FCSTD DOCUMENT  (FreeCAD 1.1R39747 (Git))
Label: Hackrf-side
License: All rights reserved
LicenseURL: https://en.wikipedia.org/wiki/All_rights_reserved
objects: Sketcher::SketchObject×3, PartDesign::Body×2, App::Point×2
note: 8 computed .brp shape members not serialized (recipe doc carries the construction recipe); baked Part::Feature solids carry a one-line shape summary decoded from their .brp

FEATURE [Sketcher::SketchObject] Sketch  label="Крепление"
  ArcFitTolerance = 1e-06
  AttachmentSupport = -> [XY_Plane]
  ExternalTypes = [0]
  FullyConstrained = true
  MakeInternals = false
  MapMode = 5
  sketch-geometry (27):
    g0: Circle CenterX=-33.5 CenterY=55.985 CenterZ=0 NormalX=0 NormalY=0 NormalZ=1 AngleXU=0 Radius=1.7
    g1: Circle CenterX=33.5 CenterY=55.985 CenterZ=0 NormalX=0 NormalY=0 NormalZ=1 AngleXU=0 Radius=1.7
    g2: LineSegment [constr] StartX=-35.2 StartY=55.985 StartZ=0 EndX=35.2 EndY=55.985 EndZ=0
    g3: GeomPoint [constr] X=-35.2 Y=55.985 Z=0
    g4: GeomPoint [constr] X=35.2 Y=55.985 Z=0
    g5: Circle CenterX=6.43685 CenterY=10.9396 CenterZ=0 NormalX=0 NormalY=0 NormalZ=1 AngleXU=0 Radius=1.7
    g6: Circle CenterX=33.5 CenterY=-55.985 CenterZ=0 NormalX=0 NormalY=0 NormalZ=1 AngleXU=0 Radius=1.7
    g7: Circle CenterX=-33.5 CenterY=-55.985 CenterZ=0 NormalX=0 NormalY=0 NormalZ=1 AngleXU=0 Radius=1.7
    g8: GeomPoint [constr] X=-34.6278 Y=57.257 Z=0
    g9: GeomPoint [constr] X=7.56463 Y=9.66755 Z=0
    g10: LineSegment [constr] StartX=-34.6278 StartY=57.257 StartZ=0 EndX=7.56463 EndY=9.66755 EndZ=0
    g11: GeomPoint [constr] X=5.56135 Y=9.48237 Z=0
    g12: LineSegment [constr] StartX=34.3755 StartY=57.4422 StartZ=0 EndX=5.56135 EndY=9.48237 EndZ=0
    g13: GeomPoint [constr] X=34.3755 Y=57.4422 Z=0
    g14: LineSegment [constr] StartX=33.5 StartY=57.685 StartZ=0 EndX=33.5 EndY=-57.685 EndZ=0
    g15: GeomPoint [constr] X=33.5 Y=57.685 Z=0
    g16: GeomPoint [constr] X=33.5 Y=-57.685 Z=0
    g17: LineSegment [constr] StartX=35.2 StartY=-55.985 StartZ=0 EndX=-35.2 EndY=-55.985 EndZ=0
    g18: LineSegment [constr] StartX=-33.5 StartY=57.685 StartZ=0 EndX=-33.5 EndY=-57.685 EndZ=0
    g19: GeomPoint [constr] X=8.12422 Y=11.1464 Z=0
    g20: GeomPoint X=0 Y=0 Z=0
    g21: Circle CenterX=-33.5 CenterY=6.045 CenterZ=0 NormalX=0 NormalY=0 NormalZ=1 AngleXU=0 Radius=1.7
    g22: GeomPoint X=-33.5 Y=4.345 Z=0
    g23: GeomPoint X=-33.5 Y=7.745 Z=0
    g24: GeomPoint X=-35.1874 Y=5.8382 Z=0
    g25: GeomPoint X=-33.5 Y=-57.685 Z=0
    g26: LineSegment [constr] StartX=-35.1874 StartY=5.8382 StartZ=0 EndX=8.12422 EndY=11.1464 EndZ=0
  constraints (63):
    c: Diameter(g0) = 3.4
    c: Horizontal(g2)
    c: PointOnObject(g0,g2)
    c: PointOnObject(g1,g2)
    c: Equal(g1,g0)
    c: DistanceX(g3,g4) = 70.4
    c: Equal(g5,g0)
    c: Equal(g6,g0)
    c: Equal(g7,g0)
    c: PointOnObject(g0,g10)
    c: PointOnObject(g5,g10)
    c: Distance(g9,g8) = 63.6
    c: PointOnObject(g5,g12)
    c: PointOnObject(g1,g12)
    c: Distance(g11,g13) = 55.95
    c: Vertical(g14)
    c: PointOnObject(g1,g14)
    c: PointOnObject(g6,g14)
    c: Horizontal(g17)
    c: PointOnObject(g6,g17)
    c: PointOnObject(g7,g17)
    c: Vertical(g18)
    c: PointOnObject(g7,g18)
    c: PointOnObject(g0,g18)
    c: Coincident(g12,g13)
    c: Coincident(g12,g11)
    c: Coincident(g10,g9)
    c: PointOnObject(g9,g5)
    c: PointOnObject(g19,g5)
    c: Coincident(g10,g8)
    c: PointOnObject(g18,g0)
    c: Coincident(g2,g3)
    c: PointOnObject(g2,g0)
    c: PointOnObject(g8,g0)
    c: PointOnObject(g14,g1)
    c: Coincident(g2,g4)
    c: PointOnObject(g2,g1)
    c: Coincident(g16,g14)
    c: PointOnObject(g14,g6)
    c: PointOnObject(g17,g6)
    c: Coincident(g15,g14)
    c: Symmetric(g1,g7,g20)
    c: Coincident(g20,g-1)
    c: Equal(g21,g0)
    c: PointOnObject(g21,g18)
    c: PointOnObject(g22,g21)
    c: PointOnObject(g24,g21)
    c: PointOnObject(g23,g21)
    c: PointOnObject(g22,g18)
    c: PointOnObject(g23,g18)
    c: DistanceY(g22,g18) = 53.34
    c: PointOnObject(g25,g7)
    c: DistanceY(g25,g23) = 65.43
    c: Coincident(g26,g24)
    c: Coincident(g26,g19)
    c: PointOnObject(g21,g26)
    c: PointOnObject(g5,g26)
    c: Coincident(g18,g25)
    c: PointOnObject(g17,g7)
    c: PointOnObject(g11,g5)
    c: Distance(g26,g26) = 43.6357
    c: PointOnObject(g12,g1)
    c: DistanceY(g18,g18) = 115.37
FEATURE [Sketcher::SketchObject] Sketch001
  ArcFitTolerance = 1e-06
  AttachmentSupport = -> [XY_Plane]
  ExternalTypes = [0]
  FullyConstrained = false
  MakeInternals = false
  MapMode = 5
  sketch-geometry (10):
    g0: LineSegment [constr] StartX=-37.5 StartY=53.5088 StartZ=0 EndX=-37.5 EndY=-53.5088 EndZ=0
    g1: LineSegment [constr] StartX=-31.0088 StartY=-60 StartZ=0 EndX=31.0088 EndY=-60 EndZ=0
    g2: LineSegment [constr] StartX=37.5 StartY=-53.5088 StartZ=0 EndX=37.5 EndY=53.5088 EndZ=0
    g3: LineSegment [constr] StartX=31.0088 StartY=60 StartZ=0 EndX=-31.0088 EndY=60 EndZ=0
    g4: ArcOfCircle [constr] CenterX=-31.0088 CenterY=53.5088 CenterZ=0 NormalX=0 NormalY=0 NormalZ=1 AngleXU=0 Radius=6.49117 StartAngle=1.5708 EndAngle=3.14159
    g5: ArcOfCircle [constr] CenterX=-31.0088 CenterY=-53.5088 CenterZ=0 NormalX=0 NormalY=0 NormalZ=1 AngleXU=0 Radius=6.49117 StartAngle=3.14159 EndAngle=4.71239
    g6: ArcOfCircle [constr] CenterX=31.0088 CenterY=-53.5088 CenterZ=0 NormalX=0 NormalY=0 NormalZ=1 AngleXU=0 Radius=6.49117 StartAngle=4.71239 EndAngle=6.28319
    g7: ArcOfCircle [constr] CenterX=31.0088 CenterY=53.5088 CenterZ=0 NormalX=0 NormalY=0 NormalZ=1 AngleXU=0 Radius=6.49117 StartAngle=3e-16 EndAngle=1.5708
    g8: GeomPoint [constr] X=-37.5 Y=60 Z=0
    g9: GeomPoint [constr] X=37.5 Y=-60 Z=0
  constraints (22):
    c: Tangent(g0,g4) = -1.5708
    c: Tangent(g0,g5) = -1.5708
    c: Tangent(g1,g5) = -1.5708
    c: Tangent(g1,g6) = -1.5708
    c: Tangent(g2,g6) = -1.5708
    c: Tangent(g2,g7) = -1.5708
    c: Tangent(g3,g7) = -1.5708
    c: Tangent(g3,g4) = -1.5708
    c: Vertical(g0)
    c: Vertical(g2)
    c: Horizontal(g1)
    c: Horizontal(g3)
    c: Equal(g4,g5)
    c: Equal(g5,g6)
    c: Equal(g6,g7)
    c: PointOnObject(g8,g0)
    c: PointOnObject(g8,g3)
    c: PointOnObject(g9,g1)
    c: PointOnObject(g9,g2)
    c: Symmetric(g4,g6,g-1)
    c: DistanceY(g9,g8) = 120
    c: DistanceX(g8,g9) = 75
FEATURE [PartDesign::Body] Body  label="Замеры"
  AllowCompound = false
  Group = -> [Sketch,Sketch001]
  Origin = -> Origin
FEATURE [Sketcher::SketchObject] Sketch002
  ArcFitTolerance = 1e-06
  AttachmentSupport = -> [XZ_Plane001]
  ExternalTypes = [0]
  FullyConstrained = false
  MakeInternals = false
  MapMode = 5
  Placement = pos=(0,0,0) rot=(1,0,0;1.5708rad)
  sketch-geometry (23):
    g0: LineSegment StartX=-36.9896 StartY=2.81128 StartZ=0 EndX=-36.9896 EndY=-13.4411 EndZ=0
    g1: LineSegment StartX=-22.1216 StartY=-28.3091 StartZ=0 EndX=25.829 EndY=-28.3091 EndZ=0
    g2: LineSegment StartX=38.9517 StartY=-12.1864 StartZ=0 EndX=38.9517 EndY=1.33855 EndZ=0
    g3: ArcOfCircle CenterX=-22.1216 CenterY=2.81128 CenterZ=0 NormalX=0 NormalY=0 NormalZ=1 AngleXU=0 Radius=14.868 StartAngle=1.52761 EndAngle=3.14159
    g4: ArcOfCircle CenterX=-22.1216 CenterY=-13.4411 CenterZ=0 NormalX=0 NormalY=0 NormalZ=1 AngleXU=0 Radius=14.868 StartAngle=3.14159 EndAngle=4.71239
    g5: ArcOfCircle CenterX=24.6534 CenterY=1.33855 CenterZ=0 NormalX=0 NormalY=0 NormalZ=1 AngleXU=0 Radius=14.2983 StartAngle=0 EndAngle=1.37697
    g6: GeomPoint [constr] X=-36.9896 Y=15.9698 Z=0
    g7: GeomPoint [constr] X=38.9517 Y=-28.3091 Z=0
    g8: LineSegment StartX=-35.4896 StartY=1.31583 StartZ=0 EndX=-35.4896 EndY=-11.9344 EndZ=0
    g9: LineSegment StartX=-20.6148 StartY=-26.8091 StartZ=0 EndX=24.329 EndY=-26.8091 EndZ=0
    g10: LineSegment StartX=40.4517 StartY=-13.6864 StartZ=0 EndX=40.4517 EndY=2.33184 EndZ=0
    g11: ArcOfCircle CenterX=-20.6148 CenterY=1.31583 CenterZ=0 NormalX=0 NormalY=0 NormalZ=1 AngleXU=0 Radius=14.8748 StartAngle=1.62897 EndAngle=3.14159
    g12: ArcOfCircle CenterX=-20.6148 CenterY=-11.9344 CenterZ=0 NormalX=0 NormalY=0 NormalZ=1 AngleXU=0 Radius=14.8748 StartAngle=3.14159 EndAngle=4.71239
    g13: ArcOfCircle CenterX=25.829 CenterY=2.33184 CenterZ=0 NormalX=0 NormalY=0 NormalZ=1 AngleXU=0 Radius=14.6227 StartAngle=0 EndAngle=1.46264
    g14: GeomPoint [constr] X=-35.4896 Y=17.4698 Z=0
    g15: GeomPoint [constr] X=40.4517 Y=-26.8091 Z=0
    g16: LineSegment StartX=-21.4797 StartY=16.1654 StartZ=0 EndX=-21.4797 EndY=17.6654 EndZ=0
    g17: LineSegment StartX=27.4075 StartY=15.3691 StartZ=0 EndX=27.4075 EndY=16.8691 EndZ=0
    g18: LineSegment [constr] StartX=-35.4896 StartY=1.31583 StartZ=0 EndX=-36.9896 EndY=1.31583 EndZ=0
    g19: LineSegment [constr] StartX=38.9517 StartY=1.33855 StartZ=0 EndX=40.4517 EndY=1.33855 EndZ=0
    g20: LineSegment [constr] StartX=-4.68607 StartY=-28.3091 StartZ=0 EndX=-4.68607 EndY=-26.8091 EndZ=0
    g21: ArcOfCircle CenterX=24.329 CenterY=-12.1864 CenterZ=0 NormalX=0 NormalY=0 NormalZ=1 AngleXU=0 Radius=14.6227 StartAngle=4.71239 EndAngle=6.28319
    g22: ArcOfCircle CenterX=25.829 CenterY=-13.6864 CenterZ=0 NormalX=0 NormalY=0 NormalZ=1 AngleXU=0 Radius=14.6227 StartAngle=4.71239 EndAngle=6.28319
  constraints (48):
    c: Tangent(g0,g3) = -1.5708
    c: Tangent(g0,g4) = -1.5708
    c: Tangent(g1,g4) = -1.5708
    c: Tangent(g2,g5) = -1.5708
    c: Vertical(g0)
    c: Horizontal(g1)
    c: Equal(g3,g4)
    c: PointOnObject(g6,g0)
    c: PointOnObject(g7,g1)
    c: PointOnObject(g7,g2)
    c: Tangent(g8,g11) = -1.5708
    c: Tangent(g8,g12) = -1.5708
    c: Tangent(g9,g12) = -1.5708
    c: Tangent(g10,g13) = -1.5708
    c: Vertical(g8)
    c: Horizontal(g9)
    c: Equal(g11,g12)
    c: PointOnObject(g14,g8)
    c: PointOnObject(g15,g9)
    c: PointOnObject(g15,g10)
    c: Vertical(g16)
    c: Vertical(g17)
    c: Distance(g16,g16) = 1.5
    c: Vertical(g2)
    c: Vertical(g10)
    c: Coincident(g16,g3)
    c: Coincident(g11,g16)
    c: Coincident(g17,g5)
    c: Coincident(g17,g13)
    c: Equal(g17,g16)
    c: Coincident(g18,g8)
    c: PointOnObject(g18,g0)
    c: Horizontal(g18)
    c: Coincident(g19,g2)
    c: PointOnObject(g19,g10)
    c: Horizontal(g19)
    c: Equal(g19,g18)
    c: Equal(g18,g16)
    c: PointOnObject(g20,g1)
    c: PointOnObject(g20,g9)
    c: Vertical(g20)
    c: Equal(g20,g18)
    c: Tangent(g22,g1) = -1.5708
    c: Tangent(g21,g9) = -1.5708
    c: Tangent(g21,g2) = -1.5708
    c: Tangent(g22,g10) = -1.5708
    c: Equal(g22,g21)
    c: Equal(g13,g22)
FEATURE [PartDesign::Body] Body001  label="Тело"
  AllowCompound = false
  Group = -> [Sketch002]
  Origin = -> Origin001
FEATURE [App::Point] Origin002  label="Origin"
  Role = Origin
FEATURE [App::Point] Origin003  label="Origin"
  Role = Origin
